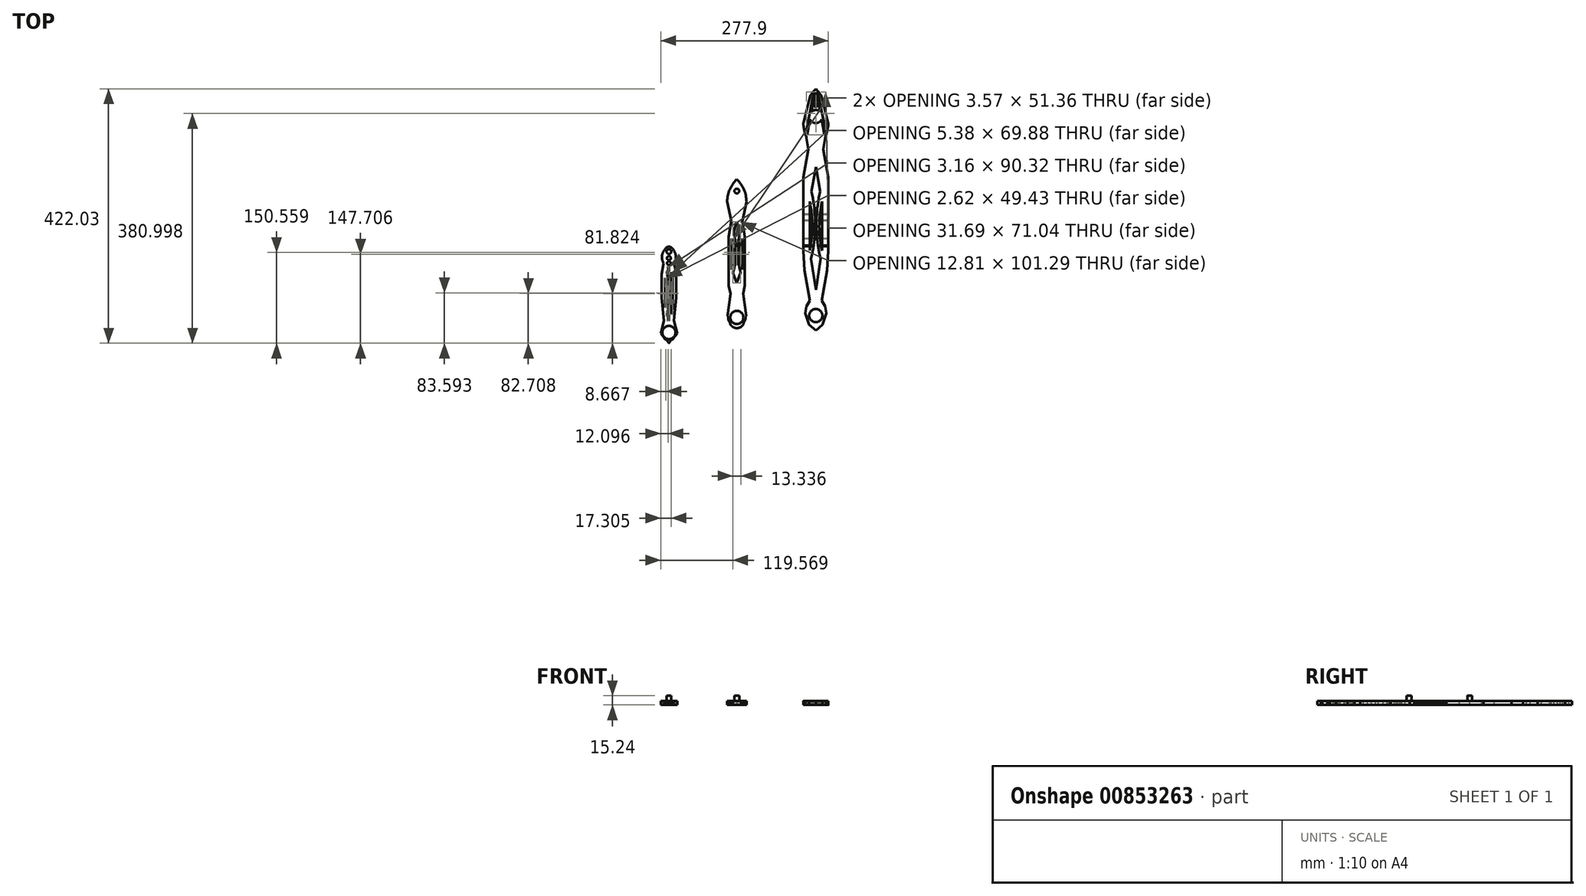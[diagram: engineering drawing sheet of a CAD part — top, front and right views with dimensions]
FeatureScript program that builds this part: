
annotation { "Feature Type Name" : "Feature", "Feature Type Description" : "" }
export const myFeature = defineFeature(function(context is Context, id is Id, definition is map)
    precondition{}
    {
        {
            var Q0;
            Q0=qCreatedBy(makeId("Top.planeOp"),FACE);
            var sketch = newSketch(context, id + "F0", { "sketchPlane" : qUnion([Q0])});
            skCircle(sketch, "E0", {"center": v(0, 129.6) * mm, "radius": 10.92 * mm});
            skArc(sketch, "E1", {"start": v(0, 175.73) * mm, "mid": v(-4.76, 170.18) * mm, "end": v(-8.96, 164.21) * mm});
            skLineSegment(sketch, "E2", {"start": v(0, 175.73) * mm, "end": v(0, -20.98) * mm});
            skArc(sketch, "E3.MirrorCS", {"start": v(0, 175.73) * mm, "mid": v(4.76, 170.18) * mm, "end": v(8.96, 164.21) * mm});
            skCircle(sketch, "E4", {"center": v(0, 148.33) * mm, "radius": 2.83 * mm});
            skCircle(sketch, "E5", {"center": v(0, 163.69) * mm, "radius": 1.4 * mm});
            skCircle(sketch, "E6", {"center": v(0, 157.29) * mm, "radius": 2.18 * mm});
            skLineSegment(sketch, "E7", {"start": v(-8.96, 164.21) * mm, "end": v(-20.73, 118.2) * mm});
            skLineSegment(sketch, "E8.MirrorCS", {"start": v(8.96, 164.21) * mm, "end": v(20.73, 118.2) * mm});
            skArc(sketch, "E9.trimOffspring", {"start": v(-20.73, 118.2) * mm, "mid": v(-18.97, 106.1) * mm, "end": v(-15.3, 94.45) * mm});
            skArc(sketch, "E10.trimOffspring", {"start": v(20.73, 118.2) * mm, "mid": v(18.97, 106.1) * mm, "end": v(15.3, 94.45) * mm});
            skLineSegment(sketch, "E11", {"start": v(-20.4, 28.7) * mm, "end": v(-20.4, -93.25) * mm});
            skLineSegment(sketch, "E12", {"start": v(-20.4, -93.25) * mm, "end": v(-18.63, -125.27) * mm});
            skLineSegment(sketch, "E13.MirrorCS", {"start": v(20.4, 28.7) * mm, "end": v(20.4, -93.25) * mm});
            skLineSegment(sketch, "E14.MirrorCS", {"start": v(20.4, -93.25) * mm, "end": v(18.63, -125.27) * mm});
            skLineSegment(sketch, "E15", {"start": v(0, 45.83) * mm, "end": v(-7.19, 5.43) * mm});
            skLineSegment(sketch, "E16", {"start": v(-10.19, -11.44) * mm, "end": v(-10.19, -92.53) * mm});
            skLineSegment(sketch, "E17", {"start": v(-7.97, -106.77) * mm, "end": v(0, -158) * mm});
            skLineSegment(sketch, "E18.MirrorCS", {"start": v(0, 45.83) * mm, "end": v(7.19, 5.43) * mm});
            skLineSegment(sketch, "E19.MirrorCS", {"start": v(10.19, -11.44) * mm, "end": v(10.19, -92.53) * mm});
            skLineSegment(sketch, "E20.MirrorCS", {"start": v(7.97, -106.77) * mm, "end": v(0, -158) * mm});
            skCircle(sketch, "E21", {"center": v(0, -200.6) * mm, "radius": 10.92 * mm});
            skLineSegment(sketch, "E22", {"start": v(-15.3, -184.95) * mm, "end": v(-17.4, -196.64) * mm});
            skLineSegment(sketch, "E23", {"start": v(-17.4, -196.64) * mm, "end": v(-10.88, -215.47) * mm});
            skLineSegment(sketch, "E24", {"start": v(-10.88, -215.47) * mm, "end": v(0, -225.4) * mm});
            skLineSegment(sketch, "E25.MirrorCS", {"start": v(15.3, -184.95) * mm, "end": v(17.4, -196.64) * mm});
            skLineSegment(sketch, "E26.MirrorCS", {"start": v(17.4, -196.64) * mm, "end": v(10.88, -215.47) * mm});
            skLineSegment(sketch, "E27.MirrorCS", {"start": v(10.88, -215.47) * mm, "end": v(0, -225.4) * mm});
            skLineSegment(sketch, "E28", {"start": v(-20.4, 28.7) * mm, "end": v(-12.15, 75.12) * mm});
            skLineSegment(sketch, "E29", {"start": v(-12.15, 75.12) * mm, "end": v(-15.3, 94.45) * mm});
            skLineSegment(sketch, "E30.MirrorCS", {"start": v(20.4, 28.7) * mm, "end": v(12.15, 75.12) * mm});
            skLineSegment(sketch, "E31.MirrorCS", {"start": v(12.15, 75.12) * mm, "end": v(15.3, 94.45) * mm});
            skPoint(sketch, "E32.MirrorCS.end.orphan", {"position": v(20.4, 44.1) * mm});
            skPoint(sketch, "E32.MirrorCS.start.orphan", {"position": v(15.3, 94.45) * mm});
            skPoint(sketch, "E33.orphan", {"position": v(-20.4, 44.1) * mm});
            skLineSegment(sketch, "E34", {"start": v(18.63, -125.27) * mm, "end": v(10.1, -175.58) * mm});
            skPoint(sketch, "E34.startSnap0", {"position": v(-5.1, -125.27) * mm});
            skLineSegment(sketch, "E35", {"start": v(10.1, -175.58) * mm, "end": v(15.3, -184.95) * mm});
            skLineSegment(sketch, "E36.MirrorCS", {"start": v(-18.63, -125.27) * mm, "end": v(-10.1, -175.58) * mm});
            skLineSegment(sketch, "E37.MirrorCS", {"start": v(-10.1, -175.58) * mm, "end": v(-15.3, -184.95) * mm});
            skLineSegment(sketch, "E38", {"start": v(-1.04, 170.22) * mm, "end": v(-7.12, 137.89) * mm});
            skLineSegment(sketch, "E39", {"start": v(1.04, 170.22) * mm, "end": v(7.12, 137.89) * mm});
            skLineSegment(sketch, "E40.trimOffspring", {"start": v(-9.65, 124.49) * mm, "end": v(-14.41, 99.18) * mm});
            skLineSegment(sketch, "E41.trimOffspring", {"start": v(9.65, 124.49) * mm, "end": v(14.41, 99.18) * mm});
            skLineSegment(sketch, "E42", {"start": v(-4.5, 162.87) * mm, "end": v(-15.85, 105.98) * mm});
            skLineSegment(sketch, "E43.MirrorCS", {"start": v(4.5, 162.87) * mm, "end": v(15.85, 105.98) * mm});
            skLineSegment(sketch, "E44", {"start": v(-15.85, 105.98) * mm, "end": v(-14.41, 99.18) * mm});
            skLineSegment(sketch, "E45", {"start": v(-1.04, 170.22) * mm, "end": v(-4.5, 162.87) * mm});
            skLineSegment(sketch, "E46.MirrorCS", {"start": v(15.85, 105.98) * mm, "end": v(14.41, 99.18) * mm});
            skLineSegment(sketch, "E47.MirrorCS", {"start": v(1.04, 170.22) * mm, "end": v(4.5, 162.87) * mm});
            skPoint(sketch, "E48.orphan", {"position": v(-2.5, 172.96) * mm});
            skPoint(sketch, "E49.orphan", {"position": v(2.5, 172.96) * mm});
            skPoint(sketch, "E50.orphan", {"position": v(-17.14, 99.5) * mm});
            skPoint(sketch, "E51.orphan", {"position": v(17.14, 99.5) * mm});
            skArc(sketch, "E52", {"start": v(-7.97, -106.77) * mm, "mid": v(-1.05, -50.72) * mm, "end": v(-7.19, 5.43) * mm});
            skArc(sketch, "E53.MirrorCS", {"start": v(7.97, -106.77) * mm, "mid": v(1.05, -50.72) * mm, "end": v(7.19, 5.43) * mm});
            skPoint(sketch, "E54.end.orphan", {"position": v(-8.72, -3.18) * mm});
            skPoint(sketch, "E54.start.orphan", {"position": v(-9.1, -99.48) * mm});
            skPoint(sketch, "E55.MirrorCS.end.orphan", {"position": v(8.72, -3.18) * mm});
            skPoint(sketch, "E55.MirrorCS.start.orphan", {"position": v(9.1, -99.48) * mm});
            skArc(sketch, "E56", {"start": v(-10.19, -92.53) * mm, "mid": v(-5.66, -51.98) * mm, "end": v(-10.19, -11.44) * mm});
            skArc(sketch, "E57.MirrorCS", {"start": v(10.19, -92.53) * mm, "mid": v(5.66, -51.98) * mm, "end": v(10.19, -11.44) * mm});
            skPoint(sketch, "E58.orphan", {"position": v(10.19, -11.44) * mm});
            skPoint(sketch, "E59.orphan", {"position": v(10.19, -92.53) * mm});
            skSolve(sketch);
        }
        {
            var Q0;
            Q0 = qSketchRegion(id + "F0", true);
            extrude(context, id + "F1", {"entities" : qUnion([Q0]), "depth" : 6.35 * mm, "offsetDistance" : 25.4 * mm});
        }
        {
            var Q0;
            Q0=qCreatedBy(makeId("Right.planeOp"),FACE);
            var sketch = newSketch(context, id + "F2", { "sketchPlane" : qUnion([Q0])});
            skLineSegment(sketch, "E60", {"start": v(-84.53, 11.53) * mm, "end": v(-84.53, 2.48) * mm});
            skLineSegment(sketch, "E61", {"start": v(-84.53, 2.48) * mm, "end": v(-73.77, 2.48) * mm});
            skLineSegment(sketch, "E62", {"start": v(-73.77, 2.48) * mm, "end": v(-73.77, 4.93) * mm});
            skLineSegment(sketch, "E63", {"start": v(-73.77, 4.93) * mm, "end": v(-43.43, 2.48) * mm});
            skLineSegment(sketch, "E64", {"start": v(-43.43, 2.48) * mm, "end": v(-43.43, 4.93) * mm});
            skLineSegment(sketch, "E65", {"start": v(-43.43, 4.93) * mm, "end": v(-32.43, 4.93) * mm});
            skLineSegment(sketch, "E66", {"start": v(-32.43, 4.93) * mm, "end": v(-32.43, -5.84) * mm});
            skLineSegment(sketch, "E67", {"start": v(-85.8, 11.53) * mm, "end": v(-85.8, 1.38) * mm});
            skLineSegment(sketch, "E68", {"start": v(-85.8, 1.38) * mm, "end": v(-72.8, 1.38) * mm});
            skLineSegment(sketch, "E69", {"start": v(-72.8, 1.38) * mm, "end": v(-72.8, 3.78) * mm});
            skLineSegment(sketch, "E70", {"start": v(-72.8, 3.78) * mm, "end": v(-42.07, 1.3) * mm});
            skLineSegment(sketch, "E71", {"start": v(-42.07, 1.3) * mm, "end": v(-42.07, 4.07) * mm});
            skLineSegment(sketch, "E72", {"start": v(-42.07, 4.07) * mm, "end": v(-33.6, 4.07) * mm});
            skLineSegment(sketch, "E73", {"start": v(-33.6, 4.07) * mm, "end": v(-33.6, -5.53) * mm});
            skLineSegment(sketch, "E74", {"start": v(-85.8, 11.53) * mm, "end": v(-84.53, 11.53) * mm});
            skLineSegment(sketch, "E75", {"start": v(-33.6, -5.53) * mm, "end": v(-32.43, -5.84) * mm});
            skSolve(sketch);
        }
        {
            var Q0;
            Q0 = qSketchRegion(id + "F2", true);
            extrude(context, id + "F3", {"entities" : qUnion([Q0]), "operationType" : NewBodyOperationType.REMOVE, "endBound" : BoundingType.SYMMETRIC, "depth" : 127 * mm, "offsetDistance" : 25.4 * mm});
        }
        {
            var Q0;
            Q0=qCreatedBy(makeId("Top.planeOp"),FACE);
            var sketch = newSketch(context, id + "F4", { "sketchPlane" : qUnion([Q0])});
            skCircle(sketch, "E76", {"center": v(-130.93, 6.06) * mm, "radius": 7.87 * mm});
            skLineSegment(sketch, "E77", {"start": v(-146.95, -11.4) * mm, "end": v(-140.3, -43.48) * mm});
            skLineSegment(sketch, "E78", {"start": v(-140.3, -43.48) * mm, "end": v(-144.22, -69.52) * mm});
            skLineSegment(sketch, "E79", {"start": v(-144.22, -69.52) * mm, "end": v(-144.22, -150.84) * mm});
            skLineSegment(sketch, "E80", {"start": v(-144.22, -150.84) * mm, "end": v(-141.54, -164.02) * mm});
            skLineSegment(sketch, "E81", {"start": v(-130.93, 6.06) * mm, "end": v(-130.93, -177.8) * mm});
            skLineSegment(sketch, "E82.MirrorCS", {"start": v(-117.64, -150.84) * mm, "end": v(-120.32, -164.02) * mm});
            skLineSegment(sketch, "E83.MirrorCS", {"start": v(-117.64, -69.52) * mm, "end": v(-117.64, -150.84) * mm});
            skLineSegment(sketch, "E84.MirrorCS", {"start": v(-121.57, -43.48) * mm, "end": v(-117.64, -69.52) * mm});
            skLineSegment(sketch, "E85.MirrorCS", {"start": v(-114.92, -11.4) * mm, "end": v(-121.57, -43.48) * mm});
            skLineSegment(sketch, "E86", {"start": v(-141.54, -164.02) * mm, "end": v(-146.57, -201.28) * mm});
            skPoint(sketch, "E87.end.orphan", {"position": v(-130.93, -227.14) * mm});
            skPoint(sketch, "E88.end.orphan", {"position": v(-144.22, -210.73) * mm});
            skPoint(sketch, "E89.orphan", {"position": v(-138.87, -177.2) * mm});
            skLineSegment(sketch, "E90.MirrorCS", {"start": v(-120.32, -164.02) * mm, "end": v(-115.3, -201.28) * mm});
            skPoint(sketch, "E91.MirrorCS.start.orphan", {"position": v(-117.64, -210.73) * mm});
            skPoint(sketch, "E92.MirrorCS.start.orphan", {"position": v(-123, -177.2) * mm});
            skPoint(sketch, "E93.end.orphan", {"position": v(-124.34, -170.62) * mm});
            skLineSegment(sketch, "E94", {"start": v(-130.93, -146.39) * mm, "end": v(-137.34, -129.63) * mm});
            skLineSegment(sketch, "E95", {"start": v(-139.38, -124.27) * mm, "end": v(-139.38, -72.91) * mm});
            skLineSegment(sketch, "E96", {"start": v(-136.26, -62.64) * mm, "end": v(-130.93, -45.1) * mm});
            skLineSegment(sketch, "E97.MirrorCS", {"start": v(-130.93, -146.39) * mm, "end": v(-124.53, -129.63) * mm});
            skLineSegment(sketch, "E98.MirrorCS", {"start": v(-122.48, -124.27) * mm, "end": v(-122.48, -72.91) * mm});
            skLineSegment(sketch, "E99.MirrorCS", {"start": v(-125.6, -62.64) * mm, "end": v(-130.93, -45.1) * mm});
            skArc(sketch, "E100", {"start": v(-137.34, -129.63) * mm, "mid": v(-132.1, -96.2) * mm, "end": v(-136.26, -62.64) * mm});
            skArc(sketch, "E101", {"start": v(-139.38, -124.27) * mm, "mid": v(-135.82, -98.6) * mm, "end": v(-139.38, -72.91) * mm});
            skArc(sketch, "E102.MirrorCS", {"start": v(-124.53, -129.63) * mm, "mid": v(-129.77, -96.2) * mm, "end": v(-125.6, -62.64) * mm});
            skArc(sketch, "E103.MirrorCS", {"start": v(-122.48, -124.27) * mm, "mid": v(-126.05, -98.6) * mm, "end": v(-122.48, -72.91) * mm});
            skPoint(sketch, "E104.orphan", {"position": v(-122.48, -72.91) * mm});
            skPoint(sketch, "E105.orphan", {"position": v(-122.48, -124.27) * mm});
            skPoint(sketch, "E106.orphan", {"position": v(-130.93, -219.51) * mm});
            skPoint(sketch, "E107.start.orphan", {"position": v(-138.87, -170.62) * mm});
            skPoint(sketch, "E108.MirrorCS.start.orphan", {"position": v(-123, -170.62) * mm});
            skLineSegment(sketch, "E109", {"start": v(-143.8, -202.85) * mm, "end": v(-145.41, -202.85) * mm});
            skLineSegment(sketch, "E110", {"start": v(-145.41, -202.85) * mm, "end": v(-146.57, -201.28) * mm});
            skLineSegment(sketch, "E111.MirrorCS", {"start": v(-116.45, -202.85) * mm, "end": v(-115.3, -201.28) * mm});
            skPoint(sketch, "E112.orphan", {"position": v(-147.84, -210.73) * mm});
            skPoint(sketch, "E113.orphan", {"position": v(-144.13, -203.5) * mm});
            skPoint(sketch, "E114.orphan", {"position": v(-146.69, -202.2) * mm});
            skPoint(sketch, "E115.orphan", {"position": v(-114.02, -210.73) * mm});
            skArc(sketch, "E116", {"start": v(-130.93, 25.4) * mm, "mid": v(-142.6, 8.6) * mm, "end": v(-146.95, -11.4) * mm});
            skArc(sketch, "E117.MirrorCS", {"start": v(-130.93, 25.4) * mm, "mid": v(-119.27, 8.6) * mm, "end": v(-114.92, -11.4) * mm});
            skPoint(sketch, "E118.orphan", {"position": v(-149.3, 0) * mm});
            skPoint(sketch, "E119.start.orphan", {"position": v(-112.56, 0) * mm});
            skCircle(sketch, "E120", {"center": v(-130.93, -203.62) * mm, "radius": 10.92 * mm});
            skPoint(sketch, "E121.MirrorCS.end.orphan", {"position": v(-130.93, -177.8) * mm});
            skArc(sketch, "E122", {"start": v(-145.41, -202.85) * mm, "mid": v(-144.66, -207.9) * mm, "end": v(-142.2, -212.4) * mm});
            skPoint(sketch, "E123.MirrorCS.end.orphan", {"position": v(-118.07, -202.85) * mm});
            skArc(sketch, "E124", {"start": v(-142.2, -212.4) * mm, "mid": v(-141.13, -216.08) * mm, "end": v(-138.26, -218.63) * mm});
            skArc(sketch, "E125.MirrorCS", {"start": v(-119.66, -212.4) * mm, "mid": v(-120.74, -216.08) * mm, "end": v(-123.6, -218.63) * mm});
            skArc(sketch, "E126.trimOffspring", {"start": v(-119.66, -212.4) * mm, "mid": v(-117.2, -207.9) * mm, "end": v(-116.45, -202.85) * mm});
            skArc(sketch, "E127", {"start": v(-138.26, -218.63) * mm, "mid": v(-130.93, -221.5) * mm, "end": v(-123.6, -218.63) * mm});
            skPoint(sketch, "E128.orphan", {"position": v(-130.93, -217.78) * mm});
            skSolve(sketch);
        }
        {
            var Q0;
            Q0 = qSketchRegion(id + "F4", true);
            var Q1;
            Q1=makeQuery(id+"F4.imprint","IMPRINT",FACE,{"disambiguationData":[TD([[makeQuery(id+"F4.imprint","IMPRINT",EDGE,{"derivedFrom":sQuery(id+"F4.wireOp",EDGE,"E76")}),1.0]])]});
            extrude(context, id + "F5", {"entities" : qUnion([Q0, Q1]), "depth" : 6.35 * mm, "offsetDistance" : 25.4 * mm});
        }
        {
            var Q0;
            Q0=makeQuery(id+"F5.opExtrude","CAP_FACE",FACE,{"disambiguationData":[OSD([sQuery(id+"F4.wireOp",EDGE,"E119"),sQuery(id+"F4.wireOp",EDGE,"E77"),sQuery(id+"F4.wireOp",EDGE,"E78"),sQuery(id+"F4.wireOp",EDGE,"E79"),sQuery(id+"F4.wireOp",EDGE,"E80"),sQuery(id+"F4.wireOp",EDGE,"E82.MirrorCS"),sQuery(id+"F4.wireOp",EDGE,"E83.MirrorCS"),sQuery(id+"F4.wireOp",EDGE,"E84.MirrorCS"),sQuery(id+"F4.wireOp",EDGE,"E85.MirrorCS"),sQuery(id+"F4.wireOp",EDGE,"E86"),sQuery(id+"F4.wireOp",EDGE,"XAiu9fB0-qCm3-ANLh-j1AY-PDe5t3VPM2Tj"),sQuery(id+"F4.wireOp",EDGE,"E90.MirrorCS"),sQuery(id+"F4.wireOp",EDGE,"E121.MirrorCS"),sQuery(id+"F4.wireOp",EDGE,"E107"),sQuery(id+"F4.wireOp",EDGE,"E108.MirrorCS"),sQuery(id+"F4.wireOp",EDGE,"G1dtL9xI-1xdn-lylE-Sato-N2u9v6iQTzqN"),sQuery(id+"F4.wireOp",EDGE,"D0fdAbw5-80RH-qEI2-oQJj-Q7Ys79AiZWxO"),sQuery(id+"F4.wireOp",EDGE,"E94"),sQuery(id+"F4.wireOp",EDGE,"E95"),sQuery(id+"F4.wireOp",EDGE,"E96"),sQuery(id+"F4.wireOp",EDGE,"E97.MirrorCS"),sQuery(id+"F4.wireOp",EDGE,"E98.MirrorCS"),sQuery(id+"F4.wireOp",EDGE,"E99.MirrorCS"),sQuery(id+"F4.wireOp",EDGE,"E100"),sQuery(id+"F4.wireOp",EDGE,"E101"),sQuery(id+"F4.wireOp",EDGE,"E102.MirrorCS"),sQuery(id+"F4.wireOp",EDGE,"E103.MirrorCS")])],"isStart":false});
            var sketch = newSketch(context, id + "F6", { "sketchPlane" : qUnion([Q0])});
            skCircle(sketch, "E129", {"center": v(-130.93, 6.06) * mm, "radius": 3.94 * mm});
            skSolve(sketch);
        }
        {
            var Q0;
            Q0 = qSketchRegion(id + "F6", true);
            extrude(context, id + "F7", {"entities" : qUnion([Q0]), "operationType" : NewBodyOperationType.ADD, "depth" : 8.9 * mm, "offsetDistance" : 25.4 * mm});
        }
        {
            var Q0;
            Q0=qCreatedBy(makeId("Top.planeOp"),FACE);
            var sketch = newSketch(context, id + "F8", { "sketchPlane" : qUnion([Q0])});
            skLineSegment(sketch, "E130", {"start": v(-243.5, -85.46) * mm, "end": v(-243.5, -220.12) * mm});
            skLineSegment(sketch, "E131", {"start": v(-252.36, -114.05) * mm, "end": v(-255.35, -131.75) * mm});
            skLineSegment(sketch, "E132", {"start": v(-255.35, -131.75) * mm, "end": v(-255.35, -171.15) * mm});
            skLineSegment(sketch, "E133", {"start": v(-255.35, -171.15) * mm, "end": v(-251.98, -208.91) * mm});
            skLineSegment(sketch, "E134.MirrorCS", {"start": v(-234.63, -114.05) * mm, "end": v(-231.63, -131.75) * mm});
            skLineSegment(sketch, "E135.MirrorCS", {"start": v(-231.63, -131.75) * mm, "end": v(-231.63, -171.15) * mm});
            skLineSegment(sketch, "E136.MirrorCS", {"start": v(-231.63, -171.15) * mm, "end": v(-235.01, -208.91) * mm});
            skCircle(sketch, "E137", {"center": v(-243.5, -95.8) * mm, "radius": 3.94 * mm});
            skArc(sketch, "E138", {"start": v(-254.08, -230.33) * mm, "mid": v(-254.14, -230.61) * mm, "end": v(-254.19, -230.9) * mm});
            skArc(sketch, "E139", {"start": v(-246.4, -241.1) * mm, "mid": v(-245.33, -243.91) * mm, "end": v(-243.5, -246.3) * mm});
            skArc(sketch, "E140.MirrorCS", {"start": v(-240.59, -241.1) * mm, "mid": v(-241.66, -243.91) * mm, "end": v(-243.5, -246.3) * mm});
            skArc(sketch, "E141.MirrorCS", {"start": v(-232.9, -230.33) * mm, "mid": v(-232.84, -230.61) * mm, "end": v(-232.8, -230.9) * mm});
            skArc(sketch, "E142", {"start": v(-251.8, -235.75) * mm, "mid": v(-251.8, -235.75) * mm, "end": v(-251.8, -235.76) * mm});
            skArc(sketch, "E143.MirrorCS", {"start": v(-235.19, -235.75) * mm, "mid": v(-235.19, -235.75) * mm, "end": v(-235.19, -235.76) * mm});
            skPoint(sketch, "E144.orphan", {"position": v(-245.95, -235.15) * mm});
            skPoint(sketch, "E145.orphan", {"position": v(-241.04, -235.15) * mm});
            skLineSegment(sketch, "E146", {"start": v(-243.5, -119.32) * mm, "end": v(-249.81, -138) * mm});
            skPoint(sketch, "E146.startSnap0", {"position": v(-233.74, -119.32) * mm});
            skLineSegment(sketch, "E147", {"start": v(-249.81, -138) * mm, "end": v(-249.81, -187.42) * mm});
            skLineSegment(sketch, "E148", {"start": v(-249.81, -187.42) * mm, "end": v(-243.5, -209.63) * mm});
            skLineSegment(sketch, "E149.MirrorCS", {"start": v(-243.5, -119.32) * mm, "end": v(-237.17, -138) * mm});
            skLineSegment(sketch, "E150.MirrorCS", {"start": v(-237.17, -138) * mm, "end": v(-237.17, -187.42) * mm});
            skLineSegment(sketch, "E151.MirrorCS", {"start": v(-237.17, -187.42) * mm, "end": v(-243.5, -209.63) * mm});
            skArc(sketch, "E152", {"start": v(-246.65, -198.53) * mm, "mid": v(-244.43, -163.6) * mm, "end": v(-246.65, -128.65) * mm});
            skArc(sketch, "E153", {"start": v(-249.81, -187.42) * mm, "mid": v(-247.2, -162.7) * mm, "end": v(-249.81, -138) * mm});
            skArc(sketch, "E154.MirrorCS", {"start": v(-240.33, -198.53) * mm, "mid": v(-242.56, -163.6) * mm, "end": v(-240.33, -128.65) * mm});
            skArc(sketch, "E155.MirrorCS", {"start": v(-237.17, -187.42) * mm, "mid": v(-239.8, -162.7) * mm, "end": v(-237.17, -138) * mm});
            skCircle(sketch, "E156", {"center": v(-243.5, -228.66) * mm, "radius": 10.92 * mm});
            skLineSegment(sketch, "E157", {"start": v(-251.98, -208.91) * mm, "end": v(-257.17, -230.33) * mm});
            skLineSegment(sketch, "E158", {"start": v(-257.17, -230.33) * mm, "end": v(-250.7, -238.87) * mm});
            skLineSegment(sketch, "E159.MirrorCS", {"start": v(-235.01, -208.91) * mm, "end": v(-229.82, -230.33) * mm});
            skLineSegment(sketch, "E160.MirrorCS", {"start": v(-229.82, -230.33) * mm, "end": v(-236.3, -238.87) * mm});
            skPoint(sketch, "E161.orphan", {"position": v(-251.14, -218.2) * mm});
            skPoint(sketch, "E162.orphan", {"position": v(-235.84, -218.2) * mm});
            skPoint(sketch, "E163.MirrorCS.end.orphan", {"position": v(-232.9, -230.33) * mm});
            skArc(sketch, "E164.trimOffspring", {"start": v(-235.18, -235.75) * mm, "mid": v(-235.18, -235.75) * mm, "end": v(-235.19, -235.75) * mm});
            skArc(sketch, "E165.trimOffspring", {"start": v(-251.8, -235.75) * mm, "mid": v(-251.8, -235.75) * mm, "end": v(-251.8, -235.75) * mm});
            skArc(sketch, "E166.trimOffspring", {"start": v(-251.26, -238.13) * mm, "mid": v(-249.26, -240.32) * mm, "end": v(-246.4, -241.1) * mm});
            skArc(sketch, "E167.trimOffspring", {"start": v(-235.73, -238.13) * mm, "mid": v(-237.73, -240.32) * mm, "end": v(-240.59, -241.1) * mm});
            skArc(sketch, "E168", {"start": v(-243.5, -85.46) * mm, "mid": v(-254.2, -97.8) * mm, "end": v(-252.36, -114.05) * mm});
            skArc(sketch, "E169.MirrorCS", {"start": v(-243.5, -85.46) * mm, "mid": v(-232.79, -97.8) * mm, "end": v(-234.63, -114.05) * mm});
            skPoint(sketch, "E170.orphan", {"position": v(-251.14, -106.89) * mm});
            skPoint(sketch, "E171.MirrorCS.end.orphan", {"position": v(-235.84, -106.89) * mm});
            skPoint(sketch, "E171.MirrorCS.start.orphan", {"position": v(-243.5, -85.46) * mm});
            skCircle(sketch, "E172", {"center": v(-243.5, -105.36) * mm, "radius": 3.33 * mm});
            skCircle(sketch, "E173", {"center": v(-243.5, -113.66) * mm, "radius": 3.04 * mm});
            skSolve(sketch);
        }
        {
            var Q0;
            Q0=makeQuery(id+"F8.imprint","IMPRINT",FACE,{"disambiguationData":[TD([[makeQuery(id+"F8.imprint","IMPRINT",EDGE,{"derivedFrom":sQuery(id+"F8.wireOp",EDGE,"E131")}),1.0]])]});
            var Q1;
            {var subQ3=sQuery(id+"F8.wireOp",EDGE,"E152");Q1=makeQuery(id+"F8.imprint","IMPRINT",FACE,{"disambiguationData":[TD([[makeQuery(id+"F8.imprint","IMPRINT",EDGE,{"derivedFrom":subQ3}),1.0]])]});}
            var Q2;
            {var subQ3=sQuery(id+"F8.wireOp",EDGE,"E154.MirrorCS");Q2=makeQuery(id+"F8.imprint","IMPRINT",FACE,{"disambiguationData":[TD([[makeQuery(id+"F8.imprint","IMPRINT",EDGE,{"derivedFrom":subQ3}),-1.0]])]});}
            var Q3;
            {var subQ0=sQuery(id+"F8.wireOp",EDGE,"E137");var subQ1=sQuery(id+"F8.wireOp",EDGE,"E130");var subQ2=makeQuery(id+"F8.imprint","INTERSECT",VERTEX,{"disambiguationData":[OD(0.0)],"derivedFrom":[subQ1,subQ0]});Q3=makeQuery(id+"F8.imprint","IMPRINT",FACE,{"disambiguationData":[TD([[makeQuery(id+"F8.imprint","IMPRINT",EDGE,{"disambiguationData":[TD([[subQ2,1.0]])],"derivedFrom":subQ1}),1.0]])]});}
            var Q4;
            {var subQ0=sQuery(id+"F8.wireOp",EDGE,"E137");var subQ1=sQuery(id+"F8.wireOp",EDGE,"E130");var subQ2=makeQuery(id+"F8.imprint","INTERSECT",VERTEX,{"disambiguationData":[OD(0.0)],"derivedFrom":[subQ1,subQ0]});Q4=makeQuery(id+"F8.imprint","IMPRINT",FACE,{"disambiguationData":[TD([[makeQuery(id+"F8.imprint","IMPRINT",EDGE,{"disambiguationData":[TD([[subQ2,1.0]])],"derivedFrom":subQ1}),-1.0]])]});}
            extrude(context, id + "F9", {"entities" : qUnion([Q0, Q1, Q2, Q3, Q4]), "depth" : 6.35 * mm, "offsetDistance" : 25.4 * mm});
        }
        {
            var Q0;
            Q0=makeQuery(id+"F9.opExtrude","CAP_FACE",FACE,{"disambiguationData":[OSD([sQuery(id+"F8.wireOp",EDGE,"E131"),sQuery(id+"F8.wireOp",EDGE,"E132"),sQuery(id+"F8.wireOp",EDGE,"E133"),sQuery(id+"F8.wireOp",EDGE,"E134.MirrorCS"),sQuery(id+"F8.wireOp",EDGE,"E135.MirrorCS"),sQuery(id+"F8.wireOp",EDGE,"E136.MirrorCS"),sQuery(id+"F8.wireOp",EDGE,"E139"),sQuery(id+"F8.wireOp",EDGE,"E140.MirrorCS"),sQuery(id+"F8.wireOp",EDGE,"E146"),sQuery(id+"F8.wireOp",EDGE,"E147"),sQuery(id+"F8.wireOp",EDGE,"E148"),sQuery(id+"F8.wireOp",EDGE,"E149.MirrorCS"),sQuery(id+"F8.wireOp",EDGE,"E150.MirrorCS"),sQuery(id+"F8.wireOp",EDGE,"E151.MirrorCS"),sQuery(id+"F8.wireOp",EDGE,"E152"),sQuery(id+"F8.wireOp",EDGE,"E153"),sQuery(id+"F8.wireOp",EDGE,"E154.MirrorCS"),sQuery(id+"F8.wireOp",EDGE,"E155.MirrorCS"),sQuery(id+"F8.wireOp",EDGE,"E156"),sQuery(id+"F8.wireOp",EDGE,"E157"),sQuery(id+"F8.wireOp",EDGE,"E158"),sQuery(id+"F8.wireOp",EDGE,"E159.MirrorCS"),sQuery(id+"F8.wireOp",EDGE,"E160.MirrorCS"),sQuery(id+"F8.wireOp",EDGE,"E166.trimOffspring"),sQuery(id+"F8.wireOp",EDGE,"E167.trimOffspring"),sQuery(id+"F8.wireOp",EDGE,"E168"),sQuery(id+"F8.wireOp",EDGE,"E169.MirrorCS"),sQuery(id+"F8.wireOp",EDGE,"E172"),sQuery(id+"F8.wireOp",EDGE,"E173")])],"isStart":false});
            var sketch = newSketch(context, id + "F10", { "sketchPlane" : qUnion([Q0])});
            skCircle(sketch, "E174", {"center": v(-243.5, -94.44) * mm, "radius": 3.94 * mm});
            skSolve(sketch);
        }
        {
            var Q0;
            Q0 = qSketchRegion(id + "F10", true);
            extrude(context, id + "F11", {"entities" : qUnion([Q0]), "operationType" : NewBodyOperationType.ADD, "depth" : 8.9 * mm, "offsetDistance" : 25.4 * mm});
        }
    });
